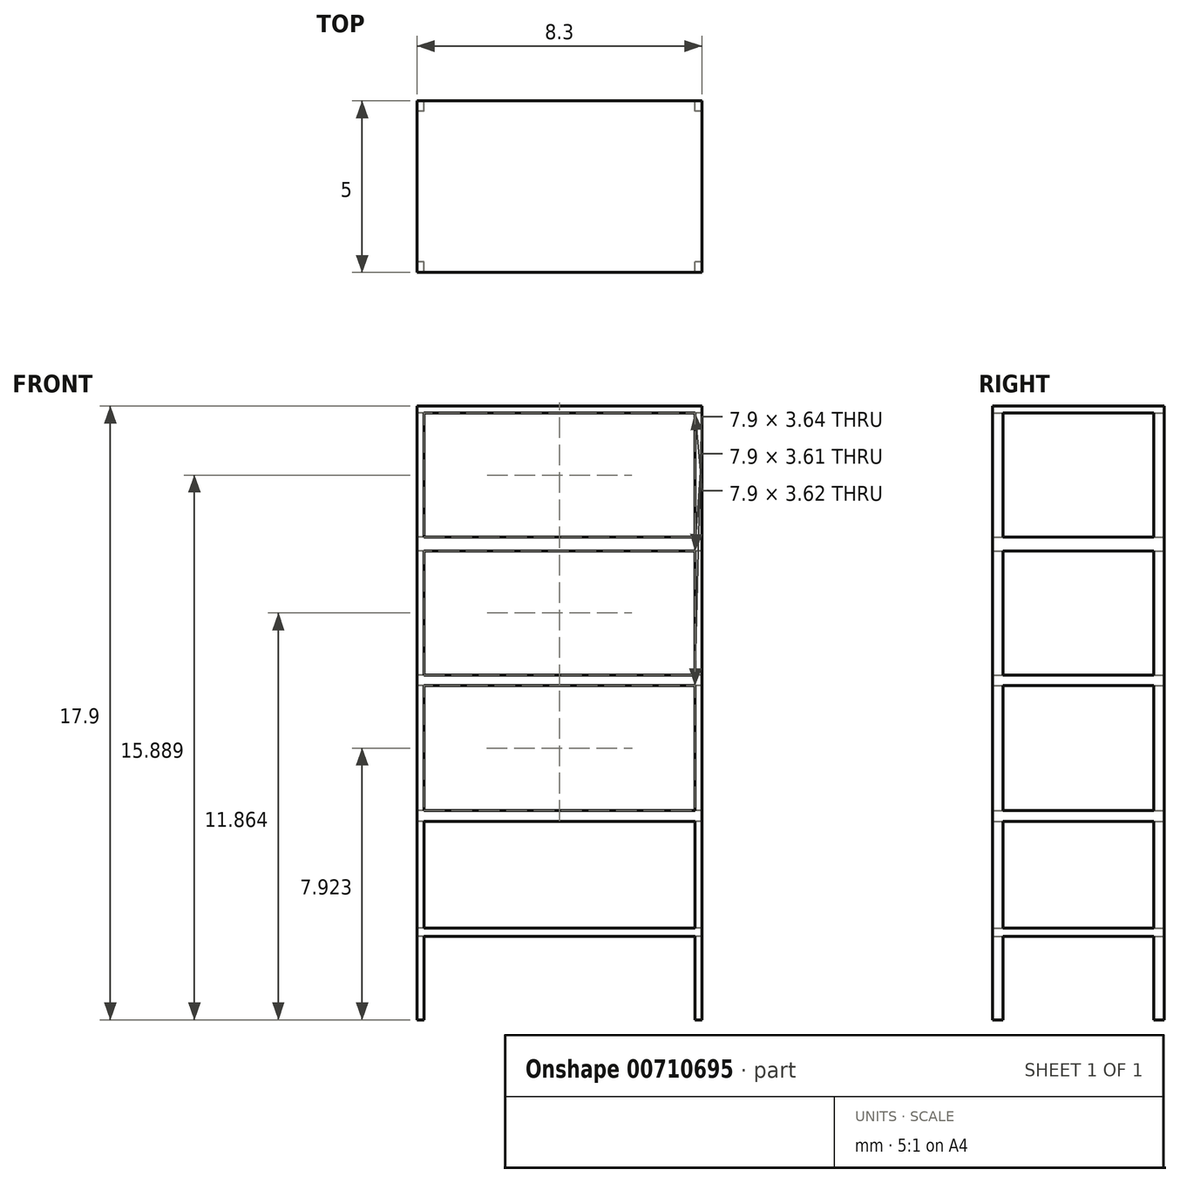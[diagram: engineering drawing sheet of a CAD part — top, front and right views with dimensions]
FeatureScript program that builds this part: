
annotation { "Feature Type Name" : "Feature", "Feature Type Description" : "" }
export const myFeature = defineFeature(function(context is Context, id is Id, definition is map)
    precondition{}
    {
        {
            var Q0;
            Q0=qCreatedBy(makeId("Top.planeOp"),FACE);
            var sketch = newSketch(context, id + "F0", { "sketchPlane" : qUnion([Q0])});
            skLineSegment(sketch, "E0.bottom", {"start": v(0, 0) * mm, "end": v(8.3, 0) * mm});
            skLineSegment(sketch, "E0.top", {"start": v(0, -5) * mm, "end": v(8.3, -5) * mm});
            skLineSegment(sketch, "E0.left", {"start": v(0, 0) * mm, "end": v(0, -5) * mm});
            skLineSegment(sketch, "E0.right", {"start": v(8.3, 0) * mm, "end": v(8.3, -5) * mm});
            skSolve(sketch);
        }
        {
            var Q0;
            Q0 = qSketchRegion(id + "F0", true);
            extrude(context, id + "F1", {"entities" : qUnion([Q0]), "depth" : 17.9 * mm, "offsetDistance" : 25 * mm});
        }
        {
            var Q0;
            Q0=makeQuery(id+"F1.opExtrude","SWEPT_FACE",FACE,{"disambiguationData":[OSD([sQuery(id+"F0.wireOp",EDGE,"E0.bottom")])]});
            var sketch = newSketch(context, id + "F2", { "sketchPlane" : qUnion([Q0])});
            skLineSegment(sketch, "E1.0", {"start": v(-8.1, 0.2) * mm, "end": v(-0.2, 0.2) * mm, "construction": true});
            skLineSegment(sketch, "E1.1", {"start": v(-8.1, 17.7) * mm, "end": v(-8.1, 0.2) * mm, "construction": true});
            skLineSegment(sketch, "E1.2", {"start": v(-0.2, 17.7) * mm, "end": v(-8.1, 17.7) * mm, "construction": true});
            skLineSegment(sketch, "E1.3", {"start": v(-0.2, 0.2) * mm, "end": v(-0.2, 17.7) * mm, "construction": true});
            skLineSegment(sketch, "E2.bottom", {"start": v(-8.1, 17.7) * mm, "end": v(-0.2, 17.7) * mm, "construction": true});
            skLineSegment(sketch, "E2.top", {"start": v(-8.1, 14.08) * mm, "end": v(-0.2, 14.08) * mm, "construction": true});
            skLineSegment(sketch, "E2.left", {"start": v(-8.1, 17.7) * mm, "end": v(-8.1, 14.08) * mm, "construction": true});
            skLineSegment(sketch, "E2.right", {"start": v(-0.2, 17.7) * mm, "end": v(-0.2, 14.08) * mm, "construction": true});
            skLineSegment(sketch, "E3.bottom", {"start": v(-8.1, 17.7) * mm, "end": v(-0.2, 17.7) * mm});
            skLineSegment(sketch, "E3.top", {"start": v(-8.1, 14.08) * mm, "end": v(-0.2, 14.08) * mm});
            skLineSegment(sketch, "E3.left", {"start": v(-8.1, 17.7) * mm, "end": v(-8.1, 14.08) * mm});
            skLineSegment(sketch, "E3.right", {"start": v(-0.2, 17.7) * mm, "end": v(-0.2, 14.08) * mm});
            skLineSegment(sketch, "E4.bottom", {"start": v(-8.1, 13.67) * mm, "end": v(-0.2, 13.67) * mm});
            skLineSegment(sketch, "E4.top", {"start": v(-8.1, 10.06) * mm, "end": v(-0.2, 10.06) * mm});
            skLineSegment(sketch, "E4.left", {"start": v(-8.1, 13.67) * mm, "end": v(-8.1, 10.06) * mm});
            skLineSegment(sketch, "E4.right", {"start": v(-0.2, 13.67) * mm, "end": v(-0.2, 10.06) * mm});
            skLineSegment(sketch, "E5.bottom", {"start": v(-8.1, 9.74) * mm, "end": v(-0.2, 9.74) * mm});
            skLineSegment(sketch, "E5.top", {"start": v(-8.1, 6.1) * mm, "end": v(-0.2, 6.1) * mm});
            skLineSegment(sketch, "E5.left", {"start": v(-8.1, 9.74) * mm, "end": v(-8.1, 6.1) * mm});
            skLineSegment(sketch, "E5.right", {"start": v(-0.2, 9.74) * mm, "end": v(-0.2, 6.1) * mm});
            skLineSegment(sketch, "E6.bottom", {"start": v(-8.1, 5.79) * mm, "end": v(-0.2, 5.79) * mm});
            skLineSegment(sketch, "E6.top", {"start": v(-8.1, 2.68) * mm, "end": v(-0.2, 2.68) * mm});
            skLineSegment(sketch, "E6.left", {"start": v(-8.1, 5.79) * mm, "end": v(-8.1, 2.68) * mm});
            skLineSegment(sketch, "E6.right", {"start": v(-0.2, 5.79) * mm, "end": v(-0.2, 2.68) * mm});
            skLineSegment(sketch, "E7.bottom", {"start": v(-8.1, 2.43) * mm, "end": v(-0.2, 2.43) * mm});
            skLineSegment(sketch, "E7.top", {"start": v(-8.1, 0) * mm, "end": v(-0.2, 0) * mm});
            skLineSegment(sketch, "E7.left", {"start": v(-8.1, 2.43) * mm, "end": v(-8.1, 0) * mm});
            skLineSegment(sketch, "E7.right", {"start": v(-0.2, 2.43) * mm, "end": v(-0.2, 0) * mm});
            skSolve(sketch);
        }
        {
            var Q0;
            Q0=makeQuery(id+"F2.imprint","IMPRINT",FACE,{"disambiguationData":[TD([[makeQuery(id+"F2.imprint","IMPRINT",EDGE,{"derivedFrom":sQuery(id+"F2.wireOp",EDGE,"E3.bottom")}),-1.0]])]});
            var Q1;
            Q1=makeQuery(id+"F2.imprint","IMPRINT",FACE,{"disambiguationData":[TD([[makeQuery(id+"F2.imprint","IMPRINT",EDGE,{"derivedFrom":sQuery(id+"F2.wireOp",EDGE,"E4.bottom")}),-1.0]])]});
            var Q2;
            Q2=makeQuery(id+"F2.imprint","IMPRINT",FACE,{"disambiguationData":[TD([[makeQuery(id+"F2.imprint","IMPRINT",EDGE,{"derivedFrom":sQuery(id+"F2.wireOp",EDGE,"E5.bottom")}),-1.0]])]});
            var Q3;
            Q3=makeQuery(id+"F2.imprint","IMPRINT",FACE,{"disambiguationData":[TD([[makeQuery(id+"F2.imprint","IMPRINT",EDGE,{"derivedFrom":sQuery(id+"F2.wireOp",EDGE,"E6.bottom")}),-1.0]])]});
            var Q4;
            Q4=makeQuery(id+"F2.imprint","IMPRINT",FACE,{"disambiguationData":[TD([[makeQuery(id+"F2.imprint","IMPRINT",EDGE,{"derivedFrom":sQuery(id+"F2.wireOp",EDGE,"E7.bottom")}),-1.0]])]});
            extrude(context, id + "F3", {"entities" : qUnion([Q0, Q1, Q2, Q3, Q4]), "operationType" : NewBodyOperationType.REMOVE, "oppositeDirection" : true, "depth" : 25 * mm, "offsetDistance" : 25 * mm});
        }
        {
            var Q0;
            Q0=qCreatedBy(makeId("Right.planeOp"),FACE);
            var sketch = newSketch(context, id + "F4", { "sketchPlane" : qUnion([Q0])});
            skLineSegment(sketch, "E8.0", {"start": v(-4.7, 17.9) * mm, "end": v(-4.7, 0) * mm, "construction": true});
            skLineSegment(sketch, "E9.0", {"start": v(-0.3, 17.9) * mm, "end": v(-0.3, 0) * mm, "construction": true});
            skLineSegment(sketch, "E10.0", {"start": v(-5, 17.7) * mm, "end": v(0, 17.7) * mm});
            skLineSegment(sketch, "E11.0", {"start": v(-5, 14.08) * mm, "end": v(0, 14.08) * mm});
            skPoint(sketch, "E12.0", {"position": v(-2.5, 13.67) * mm});
            skLineSegment(sketch, "E13.0", {"start": v(-5, 13.67) * mm, "end": v(0, 13.67) * mm});
            skLineSegment(sketch, "E14.0", {"start": v(-5, 10.06) * mm, "end": v(0, 10.06) * mm});
            skLineSegment(sketch, "E15.0", {"start": v(-5, 9.74) * mm, "end": v(0, 9.74) * mm});
            skLineSegment(sketch, "E16.bottom", {"start": v(-4.7, 17.7) * mm, "end": v(-0.3, 17.7) * mm});
            skLineSegment(sketch, "E16.top", {"start": v(-4.7, 14.08) * mm, "end": v(-0.3, 14.08) * mm});
            skLineSegment(sketch, "E16.left", {"start": v(-4.7, 17.7) * mm, "end": v(-4.7, 14.08) * mm});
            skLineSegment(sketch, "E16.right", {"start": v(-0.3, 17.7) * mm, "end": v(-0.3, 14.08) * mm});
            skLineSegment(sketch, "E17.bottom", {"start": v(-4.7, 13.67) * mm, "end": v(-0.3, 13.67) * mm});
            skLineSegment(sketch, "E17.top", {"start": v(-4.7, 10.06) * mm, "end": v(-0.3, 10.06) * mm});
            skLineSegment(sketch, "E17.left", {"start": v(-4.7, 13.67) * mm, "end": v(-4.7, 10.06) * mm});
            skLineSegment(sketch, "E17.right", {"start": v(-0.3, 13.67) * mm, "end": v(-0.3, 10.06) * mm});
            skLineSegment(sketch, "E18.0", {"start": v(-5, 6.1) * mm, "end": v(0, 6.1) * mm});
            skLineSegment(sketch, "E19.0", {"start": v(-5, 5.79) * mm, "end": v(0, 5.79) * mm});
            skLineSegment(sketch, "E20.0", {"start": v(-5, 2.68) * mm, "end": v(0, 2.68) * mm});
            skLineSegment(sketch, "E21.0", {"start": v(-5, 2.43) * mm, "end": v(0, 2.43) * mm});
            skLineSegment(sketch, "E22.bottom", {"start": v(-4.7, 9.74) * mm, "end": v(-0.3, 9.74) * mm});
            skLineSegment(sketch, "E22.top", {"start": v(-4.7, 6.1) * mm, "end": v(-0.3, 6.1) * mm});
            skLineSegment(sketch, "E22.left", {"start": v(-4.7, 9.74) * mm, "end": v(-4.7, 6.1) * mm});
            skLineSegment(sketch, "E22.right", {"start": v(-0.3, 9.74) * mm, "end": v(-0.3, 6.1) * mm});
            skLineSegment(sketch, "E23.bottom", {"start": v(-4.7, 5.79) * mm, "end": v(-0.3, 5.79) * mm});
            skLineSegment(sketch, "E23.top", {"start": v(-4.7, 2.68) * mm, "end": v(-0.3, 2.68) * mm});
            skLineSegment(sketch, "E23.left", {"start": v(-4.7, 5.79) * mm, "end": v(-4.7, 2.68) * mm});
            skLineSegment(sketch, "E23.right", {"start": v(-0.3, 5.79) * mm, "end": v(-0.3, 2.68) * mm});
            skLineSegment(sketch, "E24.bottom", {"start": v(-4.7, 2.43) * mm, "end": v(-0.3, 2.43) * mm});
            skLineSegment(sketch, "E24.top", {"start": v(-4.7, 0) * mm, "end": v(-0.3, 0) * mm});
            skLineSegment(sketch, "E24.left", {"start": v(-4.7, 2.43) * mm, "end": v(-4.7, 0) * mm});
            skLineSegment(sketch, "E24.right", {"start": v(-0.3, 2.43) * mm, "end": v(-0.3, 0) * mm});
            skSolve(sketch);
        }
        {
            var Q0;
            Q0 = qSketchRegion(id + "F4", true);
            extrude(context, id + "F5", {"entities" : qUnion([Q0]), "operationType" : NewBodyOperationType.REMOVE, "depth" : 25 * mm, "offsetDistance" : 25 * mm});
        }
    });
